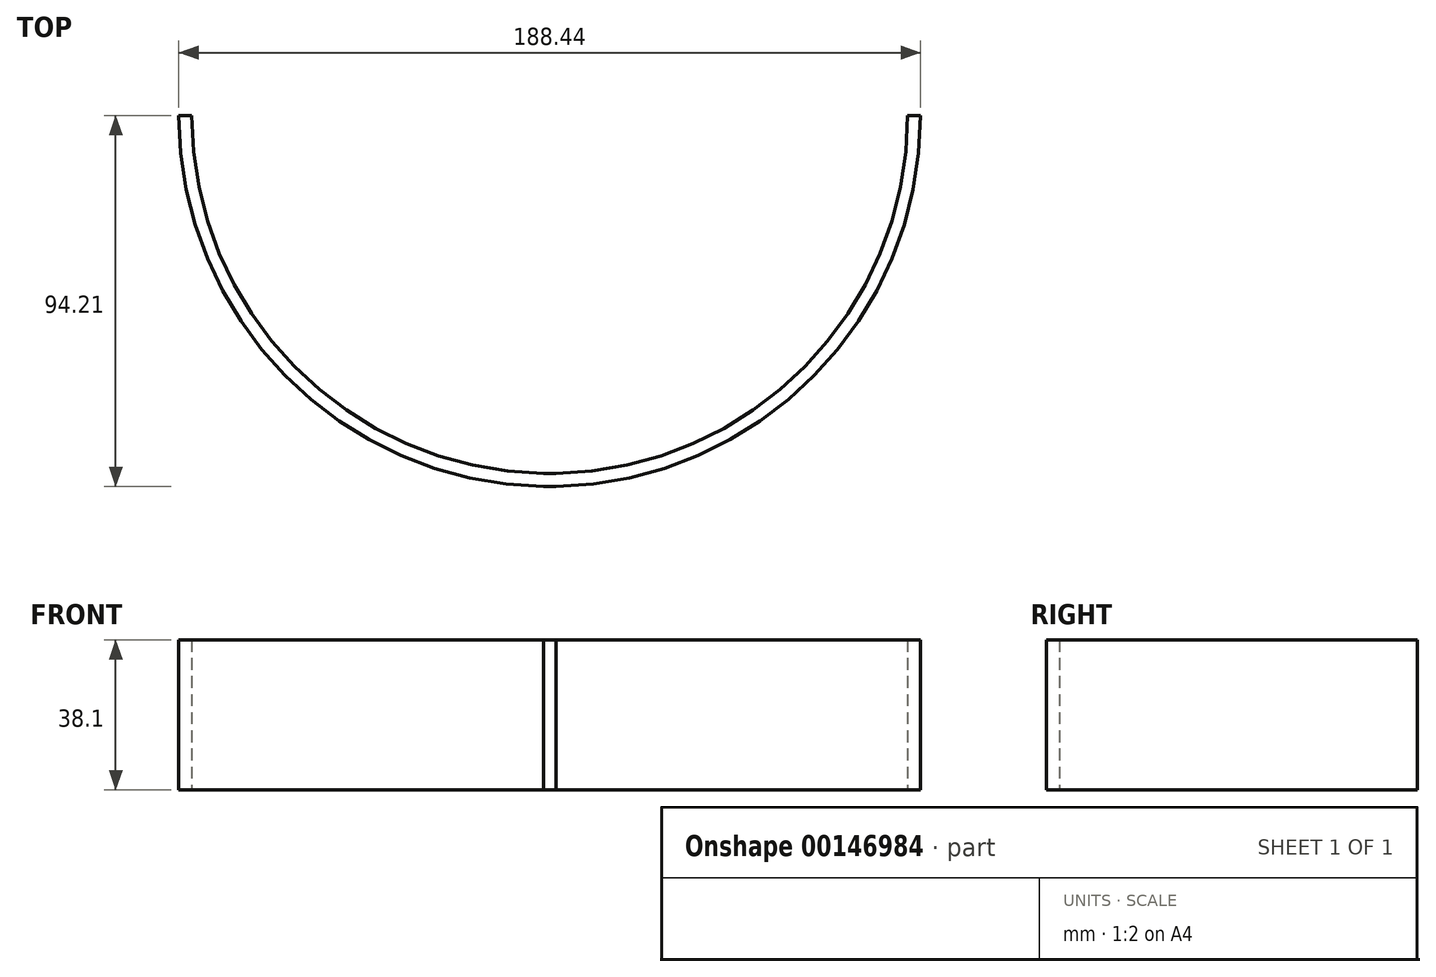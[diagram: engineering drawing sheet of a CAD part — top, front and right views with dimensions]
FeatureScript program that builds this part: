
annotation { "Feature Type Name" : "Feature", "Feature Type Description" : "" }
export const myFeature = defineFeature(function(context is Context, id is Id, definition is map)
    precondition{}
    {
        {
            var Q0;
            Q0=qCreatedBy(makeId("Top.planeOp"),FACE);
            var sketch = newSketch(context, id + "F0", { "sketchPlane" : qUnion([Q0])});
            skArc(sketch, "E0", {"start": v(-94.22, 0) * mm, "mid": v(-67.18, -66.07) * mm, "end": v(-1.56, -94.2) * mm});
            skArc(sketch, "E1", {"start": v(-90.93, 0) * mm, "mid": v(-64.85, -63.74) * mm, "end": v(-1.56, -90.92) * mm});
            skLineSegment(sketch, "E2", {"start": v(-94.22, 0) * mm, "end": v(-90.93, 0) * mm});
            skLineSegment(sketch, "E3.trimOffspring", {"start": v(90.93, 0) * mm, "end": v(94.22, 0) * mm});
            skLineSegment(sketch, "E4", {"start": v(-1.56, -90.92) * mm, "end": v(-1.56, -94.2) * mm});
            skLineSegment(sketch, "E5", {"start": v(1.56, -90.92) * mm, "end": v(1.56, -94.2) * mm});
            skArc(sketch, "E6.trimOffspring", {"start": v(1.56, -90.92) * mm, "mid": v(64.85, -63.74) * mm, "end": v(90.93, 0) * mm});
            skArc(sketch, "E7.trimOffspring", {"start": v(1.56, -94.2) * mm, "mid": v(67.18, -66.07) * mm, "end": v(94.22, 0) * mm});
            skLineSegment(sketch, "E8", {"start": v(-1.56, -94.2) * mm, "end": v(1.56, -94.2) * mm});
            skLineSegment(sketch, "E9", {"start": v(-1.56, -90.92) * mm, "end": v(1.56, -90.92) * mm});
            skSolve(sketch);
        }
        {
            var Q0;
            Q0 = qSketchRegion(id + "F0", true);
            extrude(context, id + "F1", {"entities" : qUnion([Q0]), "depth" : 38.1 * mm});
        }
    });
